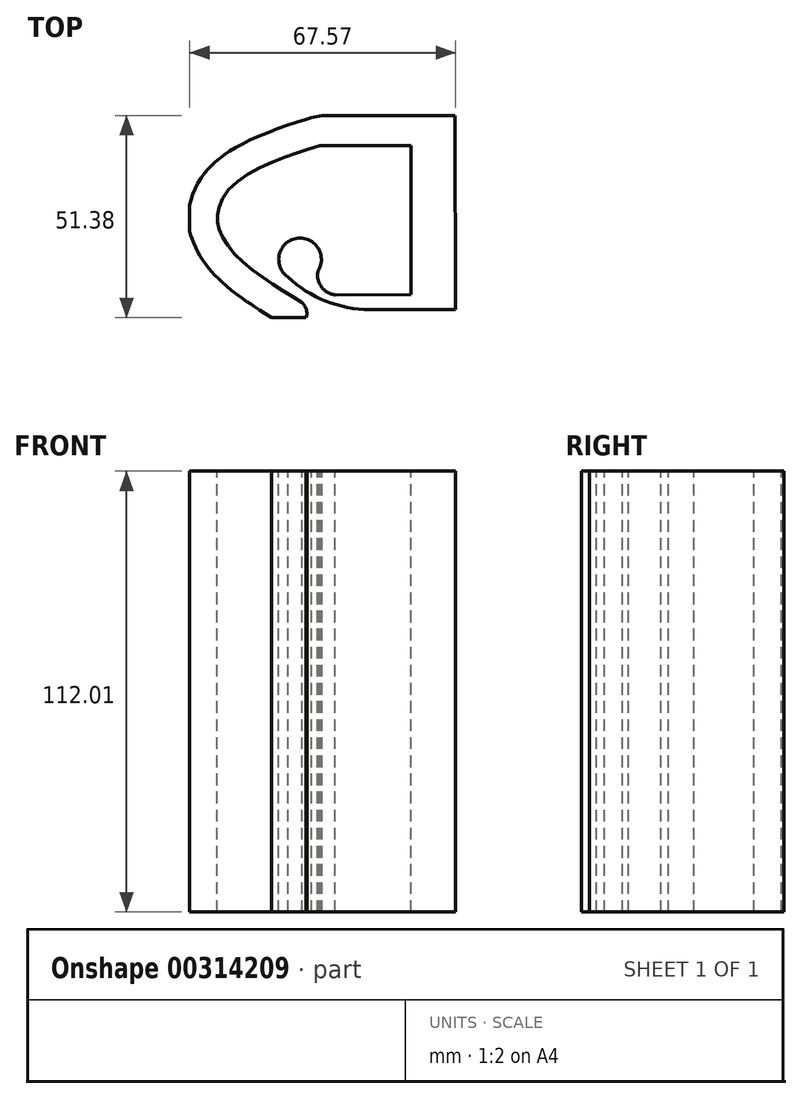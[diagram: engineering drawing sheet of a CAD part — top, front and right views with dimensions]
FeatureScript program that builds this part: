
annotation { "Feature Type Name" : "Feature", "Feature Type Description" : "" }
export const myFeature = defineFeature(function(context is Context, id is Id, definition is map)
    precondition{}
    {
        {
            var Q0;
            Q0=qCreatedBy(makeId("Top.planeOp"),FACE);
            var sketch = newSketch(context, id + "F0", { "sketchPlane" : qUnion([Q0])});
            skLineSegment(sketch, "E0.bottom", {"start": v(-34.55, 26.5) * mm, "end": v(34.55, 26.5) * mm});
            skLineSegment(sketch, "E0.top", {"start": v(-34.55, -26.5) * mm, "end": v(34.55, -26.5) * mm});
            skLineSegment(sketch, "E0.left", {"start": v(-34.55, 26.5) * mm, "end": v(-34.55, -26.5) * mm});
            skLineSegment(sketch, "E0.right", {"start": v(34.55, 26.5) * mm, "end": v(34.55, -26.5) * mm});
            skPoint(sketch, "E0.middle", {"position": v(0, 0) * mm});
            skLineSegment(sketch, "E1", {"start": v(32.92, 24.87) * mm, "end": v(33.02, -24.44) * mm});
            skLineSegment(sketch, "E2", {"start": v(33.02, -24.44) * mm, "end": v(11.27, -24.44) * mm});
            skLineSegment(sketch, "E3", {"start": v(32.92, 24.87) * mm, "end": v(-0.87, 24.87) * mm});
            skLineSegment(sketch, "E4", {"start": v(-1.48, 17.22) * mm, "end": v(21.64, 17.27) * mm});
            skLineSegment(sketch, "E5", {"start": v(21.64, 17.27) * mm, "end": v(21.72, -20.67) * mm});
            skLineSegment(sketch, "E6", {"start": v(21.72, -20.67) * mm, "end": v(2.4, -20.7) * mm});
            skArc(sketch, "E7", {"start": v(-1.2, -18.5) * mm, "mid": v(0.37, -20) * mm, "end": v(2.4, -20.7) * mm});
            skArc(sketch, "E8", {"start": v(-1.2, -18.5) * mm, "mid": v(-1.96, -16.63) * mm, "end": v(-1.92, -14.62) * mm});
            skArc(sketch, "E9", {"start": v(-1.92, -14.62) * mm, "mid": v(-7.55, -6.4) * mm, "end": v(-9.6, -16.15) * mm});
            skPoint(sketch, "E9.second.point", {"position": v(-11.09, -8.83) * mm});
            skPoint(sketch, "E9.third.point", {"position": v(-9.6, -16.15) * mm});
            skArc(sketch, "E10", {"start": v(11.27, -24.44) * mm, "mid": v(0.04, -22.3) * mm, "end": v(-9.6, -16.15) * mm});
            skFitSpline(sketch, "E11", {"points": [v(-1.48, 17.22) * mm, v(-12.86, 13.33) * mm, v(-24.24, 6.44) * mm, v(-27.44, 0) * mm, v(-27.12, -3.66) * mm, v(-23.6, -9.75) * mm, v(-14.95, -16.96) * mm, v(-5.94, -22.7) * mm], "startDerivative": vector(-67.1, -20.5) * mm, "endDerivative": vector(57.24, -35.21) * mm});
            skFitSpline(sketch, "E12.0", {"points": [v(-3.63, 24.27) * mm, v(-5.03, 23.84) * mm, v(-7.9, 22.96) * mm, v(-11.72, 21.68) * mm, v(-14.53, 20.6) * mm, v(-16.18, 19.93) * mm, v(-17.87, 19.2) * mm, v(-20.03, 18.2) * mm, v(-22.2, 17.06) * mm, v(-23.92, 16.04) * mm, v(-25.2, 15.21) * mm, v(-26.45, 14.32) * mm, v(-27.48, 13.5) * mm, v(-28.27, 12.8) * mm, v(-28.86, 12.25) * mm, v(-29.44, 11.67) * mm, v(-30.18, 10.85) * mm, v(-31.02, 9.8) * mm, v(-31.9, 8.53) * mm, v(-32.65, 7.25) * mm, v(-33.28, 5.96) * mm, v(-33.8, 4.7) * mm, v(-34.21, 3.44) * mm, v(-34.47, 2.42) * mm, v(-34.64, 1.61) * mm, v(-34.74, 1.02) * mm, v(-34.82, 0.4) * mm, v(-34.9, -0.43) * mm, v(-34.93, -1.5) * mm, v(-34.85, -2.8) * mm, v(-34.65, -4.05) * mm, v(-34.4, -5.01) * mm, v(-34.2, -5.73) * mm, v(-33.97, -6.42) * mm, v(-33.64, -7.29) * mm, v(-33.2, -8.33) * mm, v(-32.67, -9.4) * mm, v(-32.1, -10.46) * mm, v(-31.44, -11.53) * mm, v(-30.71, -12.6) * mm, v(-30.04, -13.5) * mm, v(-29.47, -14.2) * mm, v(-28.87, -14.92) * mm, v(-28.1, -15.76) * mm, v(-27.14, -16.72) * mm, v(-26.16, -17.63) * mm, v(-24.83, -18.8) * mm, v(-23.14, -20.15) * mm, v(-21.45, -21.4) * mm, v(-20.1, -22.34) * mm, v(-19.12, -23.02) * mm, v(-18.15, -23.68) * mm, v(-16.87, -24.53) * mm, v(-15.29, -25.56) * mm, v(-12.8, -27.13) * mm, v(-10.99, -28.24) * mm, v(-9.8, -28.97) * mm]});
            skLineSegment(sketch, "E13", {"start": v(-0.87, 24.87) * mm, "end": v(-3.63, 24.27) * mm});
            skArc(sketch, "E14", {"start": v(-9.8, -28.97) * mm, "mid": v(-5.33, -27.4) * mm, "end": v(-5.94, -22.7) * mm});
            skSolve(sketch);
        }
        {
            var Q0;
            Q0=makeQuery(id+"F0.imprint","IMPRINT",FACE,{"disambiguationData":[TD([[makeQuery(id+"F0.imprint","IMPRINT",EDGE,{"derivedFrom":sQuery(id+"F0.wireOp",EDGE,"E1")}),-1.0]])]});
            extrude(context, id + "F1", {"entities" : qUnion([Q0]), "oppositeDirection" : true, "depth" : 112.01 * mm});
        }
    });
